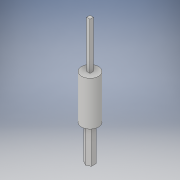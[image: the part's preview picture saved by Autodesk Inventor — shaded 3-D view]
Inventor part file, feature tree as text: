
AUTODESK INVENTOR PART (.ipt)
format: ipt  version: 2018 (Build 220112000, 112)  size: 113,152 bytes
history: native  units: in
note: dims shown in document units (in); Inventor stores cm internally (conversion verified against a paired STEP export)
features: extrude x3, sketch x3
ambient origin geometry x8: Origin, YZ Plane, XZ Plane, XY Plane, X Axis, Y Axis, Z Axis, Center Point
bodies: Solid1 (feature_tree)
feature tree (6):
  extrude  "Extrusion1"  Depth=1.5in TaperAngle=0.0deg
  extrude  "Extrusion2"  Depth=1.875in TaperAngle=0.0deg
  extrude  "Extrusion3"  Depth=2.0in TaperAngle=0.0deg
  sketch  "Sketch1"  dims[d0=0.325in d1=1.5in d2=0.0in]
  sketch  "Sketch2"  dims[d3=0.725in d4=1.875in d5=0.0in]
  sketch  "Sketch3"  dims[d6=0.145in d7=2.0in d8=0.0in]
